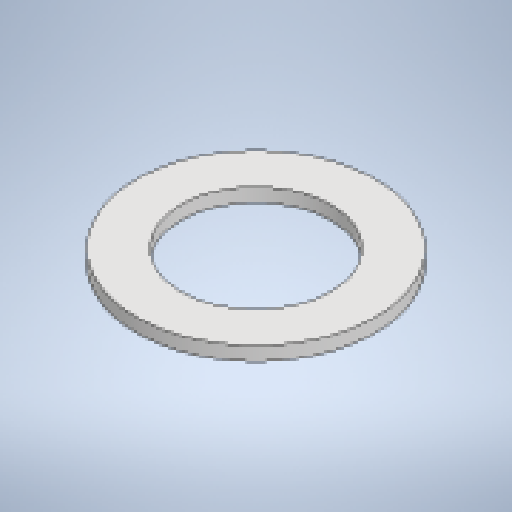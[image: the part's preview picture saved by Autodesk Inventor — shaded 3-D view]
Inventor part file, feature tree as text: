
AUTODESK INVENTOR PART (.ipt)
format: ipt  version: 2025 (Build 290162010, 162A)  size: 176,128 bytes
history: native  units: mm
features: other x2, sheet_metal_op x1, sketch x1
ambient origin geometry x8: Origin, YZ Plane, XZ Plane, XY Plane, X Axis, Y Axis, Z Axis, Center Point
bodies: Body1 (feature_tree)
feature tree (4):
  sheet_metal_op  "Face2"
  sketch  "Sketch2"  dims[d14=8.0mm d25=88.0mm d27=140.0mm]
  other  "Plate2"
  other  "Definition1"
